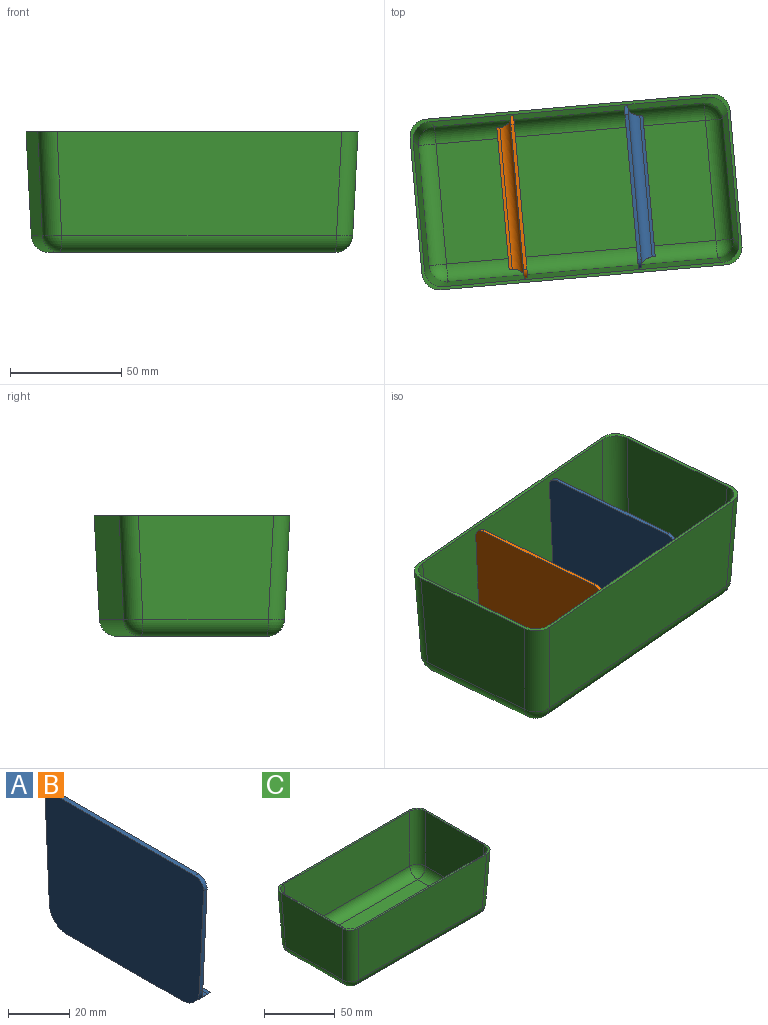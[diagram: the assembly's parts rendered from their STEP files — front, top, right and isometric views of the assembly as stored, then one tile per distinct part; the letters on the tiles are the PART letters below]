
ASSEMBLY  parts=3 mates=2
PART A: 13 faces, bbox 8x73.2x53 mm
  f0: plane 53.34x8mm, normal (0,0,-1), area 426.7mm2, adj f1,f5,f8,f9
  f1: plane 63.92x2mm, normal (1,0,0), area 121.2mm2, adj f0,f2,f8,f9
  f2: plane 63.92x1.4mm, normal (0,0,1), area 89.5mm2, adj f1,f8,f9,f10
  f3: plane 73.21x46mm, normal (1,0,0), area 3278.1mm2, adj f4,f6,f7,f8,f9,f10,f11,f12
  f4: plane 65.21x1.6mm, normal (0,0,1), area 104.3mm2, adj f3,f5,f11,f12
  f5: plane 73.21x53mm, normal (-1,0,0), area 3736.1mm2, adj f0,f4,f6,f7,f8,f9,f11,f12
  f6: plane 41.19x1.94mm, normal (0,-1,-0.05), area 66mm2, adj f3,f5,f9,f12
  f7: plane 41.19x1.94mm, normal (0,1,-0.05), area 66mm2, adj f3,f5,f8,f11
  f8: cylinder r=8mm len=8mm, axis (1,0,0), area 63.5mm2, adj f0,f1,f2,f3,f5,f7,f10
  f9: cylinder r=8mm len=8mm, axis (1,0,0), area 63.5mm2, adj f0,f1,f2,f3,f5,f6,f10
  f10: cylinder r=5mm len=69.21mm, axis (0,1,0), area 522.3mm2, adj f2,f3,f8,f9
  f11: cylinder r=4mm len=4.19mm, axis (-1,0,0), area 10.4mm2, adj f3,f4,f5,f7
  f12: cylinder r=4mm len=4.19mm, axis (-1,0,0), area 10.4mm2, adj f3,f4,f5,f6
PART B: same geometry as A
PART C: 35 faces, bbox 144.6x77.1x54.5 mm
  f0: plane 61.12x46.68mm, normal (1,0,-0.05), area 2753.1mm2, adj f8,f13,f16,f26
  f1: plane 128.62x46.68mm, normal (0,1,-0.05), area 5907.3mm2, adj f8,f13,f14,f22
  f2: plane 61.12x46.68mm, normal (-1,0,-0.05), area 2753.1mm2, adj f8,f14,f15,f19
  f3: plane 58.52x45.38mm, normal (1,0,0.05), area 2561.1mm2, adj f8,f9,f12,f32
  f4: plane 126.02x45.38mm, normal (0,-1,0.05), area 5627.4mm2, adj f8,f9,f10,f28
  f5: plane 58.52x45.38mm, normal (-1,0,0.05), area 2561.1mm2, adj f8,f10,f11,f29
  f6: plane 126.02x45.38mm, normal (0,1,0.05), area 5627.4mm2, adj f8,f11,f12,f33
  f7: plane 128.62x46.68mm, normal (0,-1,-0.05), area 5907.3mm2, adj f8,f15,f16,f23
  f8: plane 144.6x77.1mm, normal (0,0,1), area 569.7mm2, adj f0,f1,f2,f3,f4,f5,f6,f7
  f9: cylinder r=8mm len=45.69mm, axis (0.05,-0.05,-1), area 572mm2, adj f3,f4,f8,f30
  f10: cylinder r=8mm len=45.69mm, axis (-0.05,-0.05,-1), area 572mm2, adj f4,f5,f8,f27
  f11: cylinder r=8mm len=45.69mm, axis (-0.05,0.05,-1), area 572mm2, adj f5,f6,f8,f31
  f12: cylinder r=8mm len=45.69mm, axis (0.05,0.05,-1), area 572mm2, adj f3,f6,f8,f34
  f13: cylinder r=8mm len=46.99mm, axis (0.05,0.05,1), area 588.3mm2, adj f0,f1,f8,f24
  f14: cylinder r=8mm len=46.99mm, axis (-0.05,0.05,1), area 588.3mm2, adj f1,f2,f8,f20
  f15: cylinder r=8mm len=46.99mm, axis (-0.05,-0.05,1), area 588.3mm2, adj f2,f7,f8,f21
  f16: cylinder r=8mm len=46.99mm, axis (0.05,-0.05,1), area 588.3mm2, adj f0,f7,f8,f25
  f17: plane 121.74x54.24mm, normal (0,0,1), area 6602.8mm2, adj f28,f29,f32,f33
  f18: plane 124.22x56.72mm, normal (0,0,-1), area 7044.9mm2, adj f19,f22,f23,f26
  f19: cylinder r=8mm len=56.72mm, axis (0,1,0), area 691.3mm2, adj f2,f18,f20,f21
  f20: sphere r=8mm, area 94.5mm2, adj f14,f19,f22
  f21: sphere r=8mm, area 94.5mm2, adj f15,f19,f23
  f22: cylinder r=8mm len=124.22mm, axis (1,0,0), area 1514.1mm2, adj f1,f18,f20,f24
  f23: cylinder r=8mm len=124.22mm, axis (1,0,0), area 1514.1mm2, adj f7,f18,f21,f25
  f24: sphere r=8mm, area 94.5mm2, adj f13,f22,f26
  f25: sphere r=8mm, area 94.5mm2, adj f16,f23,f26
  f26: cylinder r=8mm len=56.72mm, axis (0,-1,0), area 691.3mm2, adj f0,f18,f24,f25
  f27: sphere r=8mm, area 94.5mm2, adj f10,f28,f29
  f28: cylinder r=8mm len=121.74mm, axis (-1,0,0), area 1483.9mm2, adj f4,f17,f27,f30
  f29: cylinder r=8mm len=54.24mm, axis (0,-1,0), area 661.1mm2, adj f5,f17,f27,f31
  f30: sphere r=8mm, area 94.5mm2, adj f9,f28,f32
  f31: sphere r=8mm, area 94.5mm2, adj f11,f29,f33
  f32: cylinder r=8mm len=54.24mm, axis (0,-1,0), area 661.1mm2, adj f3,f17,f30,f34
  f33: cylinder r=8mm len=121.74mm, axis (-1,0,0), area 1483.9mm2, adj f6,f17,f31,f34
  f34: sphere r=8mm, area 94.5mm2, adj f12,f32,f33
PLACE A rot(axis=(0,0,1),5deg) t=(24.05,6.91,-15.91)mm
PLACE B rot(axis=(0,0,-1),175deg) t=(-25.76,2.55,-15.91)mm
PLACE C rot(axis=(0,0,1),5deg) t=(-0.85,4.73,-15.91)mm
MATE revolute B.f0 <-> C.f17  axis (0,0,1) through (-25.76,2.55,-15.91)mm
MATE fastened A.f0 <-> C.f17  axis (0,0,1) through (24.05,6.91,-15.91)mm
